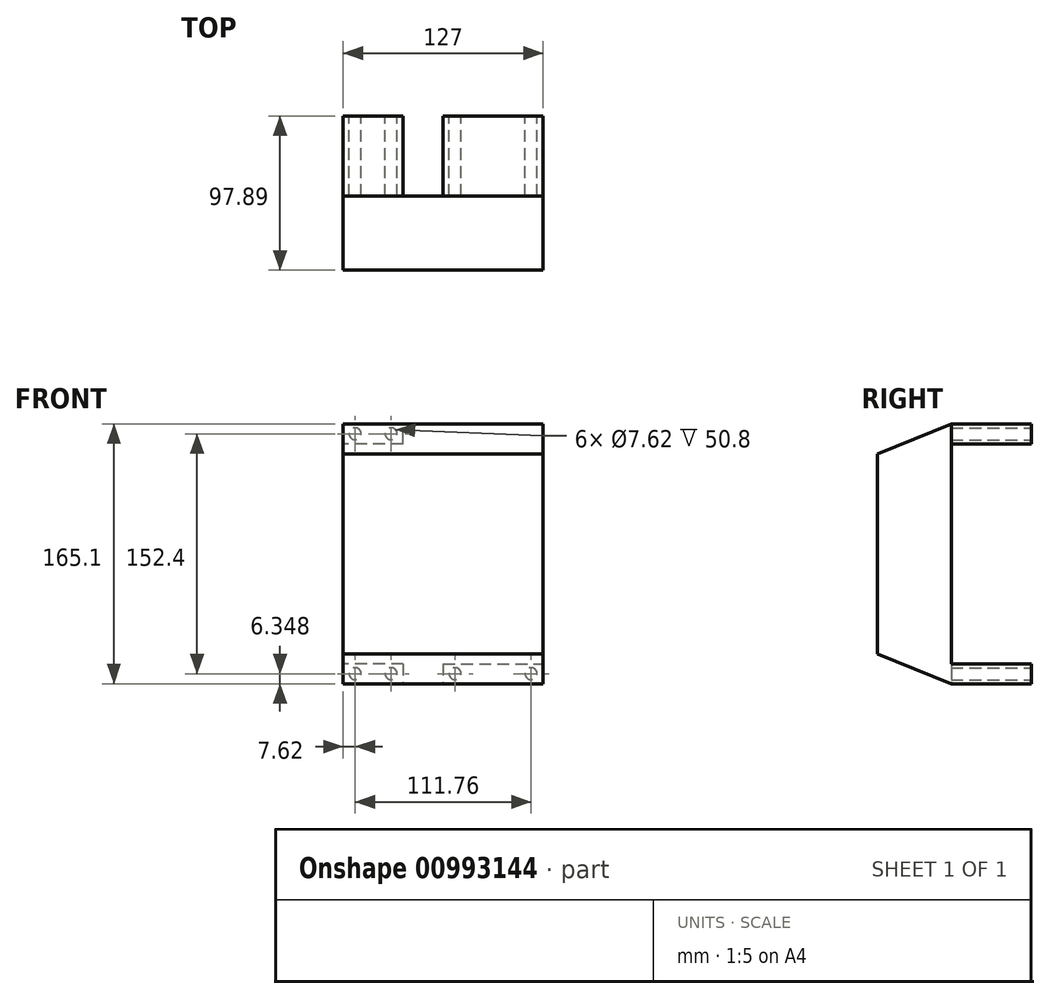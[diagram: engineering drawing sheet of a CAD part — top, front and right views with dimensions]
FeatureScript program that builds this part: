
annotation { "Feature Type Name" : "Feature", "Feature Type Description" : "" }
export const myFeature = defineFeature(function(context is Context, id is Id, definition is map)
    precondition{}
    {
        {
            var Q0;
            Q0=qCreatedBy(makeId("Right.planeOp"),FACE);
            var sketch = newSketch(context, id + "F0", { "sketchPlane" : qUnion([Q0])});
            skLineSegment(sketch, "E0", {"start": v(37.9, 107.88) * mm, "end": v(37.9, -57.22) * mm});
            skLineSegment(sketch, "E1", {"start": v(37.9, 107.88) * mm, "end": v(-9.2, 88.83) * mm});
            skLineSegment(sketch, "E2", {"start": v(-9.2, 88.83) * mm, "end": v(-9.2, -38.17) * mm});
            skLineSegment(sketch, "E3", {"start": v(-9.2, -38.17) * mm, "end": v(37.9, -57.22) * mm});
            skLineSegment(sketch, "E4.bottom", {"start": v(37.9, -57.22) * mm, "end": v(88.7, -57.22) * mm});
            skLineSegment(sketch, "E4.top", {"start": v(37.9, -44.52) * mm, "end": v(88.7, -44.52) * mm});
            skLineSegment(sketch, "E4.left", {"start": v(37.9, -57.22) * mm, "end": v(37.9, -44.52) * mm});
            skLineSegment(sketch, "E4.right", {"start": v(88.7, -57.22) * mm, "end": v(88.7, -44.52) * mm});
            skSolve(sketch);
        }
        {
            var Q0;
            Q0=makeQuery(id+"F0.imprint","IMPRINT",FACE,{"disambiguationData":[TD([[makeQuery(id+"F0.imprint","IMPRINT",EDGE,{"derivedFrom":sQuery(id+"F0.wireOp",EDGE,"E0")}),-1.0]])]});
            extrude(context, id + "F1", {"entities" : qUnion([Q0]), "depth" : 127 * mm, "offsetDistance" : 25.4 * mm});
        }
        {
            var Q0;
            Q0=makeQuery(id+"F0.imprint","IMPRINT",FACE,{"disambiguationData":[TD([[makeQuery(id+"F0.imprint","IMPRINT",EDGE,{"derivedFrom":sQuery(id+"F0.wireOp",EDGE,"E4.bottom")}),1.0]])]});
            extrude(context, id + "F2", {"entities" : qUnion([Q0]), "operationType" : NewBodyOperationType.ADD, "depth" : 38.1 * mm, "offsetDistance" : 25.4 * mm});
        }
        {
            var Q0;
            Q0=makeQuery(id+"F1.opExtrude","SWEPT_FACE",FACE,{"disambiguationData":[OSD([sQuery(id+"F0.wireOp",EDGE,"E0"),sQuery(id+"F0.wireOp",EDGE,"E4.left")])]});
            var sketch = newSketch(context, id + "F3", { "sketchPlane" : qUnion([Q0])});
            skLineSegment(sketch, "E5.bottom", {"start": v(-63.5, -44.52) * mm, "end": v(-127, -44.52) * mm});
            skLineSegment(sketch, "E5.top", {"start": v(-63.5, -57.22) * mm, "end": v(-127, -57.22) * mm});
            skLineSegment(sketch, "E5.left", {"start": v(-63.5, -44.52) * mm, "end": v(-63.5, -57.22) * mm});
            skLineSegment(sketch, "E5.right", {"start": v(-127, -44.52) * mm, "end": v(-127, -57.22) * mm});
            skLineSegment(sketch, "E6.bottom", {"start": v(-38.1, 95.18) * mm, "end": v(0, 95.18) * mm});
            skLineSegment(sketch, "E6.top", {"start": v(-38.1, 107.88) * mm, "end": v(0, 107.88) * mm});
            skLineSegment(sketch, "E6.left", {"start": v(-38.1, 95.18) * mm, "end": v(-38.1, 107.88) * mm});
            skLineSegment(sketch, "E6.right", {"start": v(0, 95.18) * mm, "end": v(0, 107.88) * mm});
            skSolve(sketch);
        }
        {
            var Q0;
            Q0=makeQuery(id+"F3.imprint","IMPRINT",FACE,{"disambiguationData":[TD([[makeQuery(id+"F3.imprint","IMPRINT",EDGE,{"derivedFrom":sQuery(id+"F3.wireOp",EDGE,"E5.bottom")}),1.0]])]});
            var Q1;
            Q1=makeQuery(id+"F3.imprint","IMPRINT",FACE,{"disambiguationData":[TD([[makeQuery(id+"F3.imprint","IMPRINT",EDGE,{"derivedFrom":sQuery(id+"F3.wireOp",EDGE,"tAGeQwlt-6s59-XwvX-LVoE-sqzA5QCWcFZO.bottom")}),-1.0]])]});
            var Q2;
            Q2=makeQuery(id+"F3.imprint","IMPRINT",FACE,{"disambiguationData":[TD([[makeQuery(id+"F3.imprint","IMPRINT",EDGE,{"derivedFrom":sQuery(id+"F3.wireOp",EDGE,"E6.bottom")}),1.0]])]});
            extrude(context, id + "F4", {"entities" : qUnion([Q0, Q1, Q2]), "operationType" : NewBodyOperationType.ADD, "depth" : 50.8 * mm, "offsetDistance" : 25.4 * mm});
        }
        {
            var Q0;
            Q0=makeQuery(id+"F4.opExtrude","CAP_FACE",FACE,{"disambiguationData":[OSD([sQuery(id+"F3.wireOp",EDGE,"E6.bottom"),sQuery(id+"F3.wireOp",EDGE,"E6.top"),sQuery(id+"F3.wireOp",EDGE,"E6.left"),sQuery(id+"F3.wireOp",EDGE,"E6.right")])],"isStart":false});
            var sketch = newSketch(context, id + "F5", { "sketchPlane" : qUnion([Q0])});
            skCircle(sketch, "E7", {"center": v(-30.48, 101.53) * mm, "radius": 3.81 * mm});
            skPoint(sketch, "E7.centerSnap0", {"position": v(-38.1, 101.53) * mm});
            skCircle(sketch, "E8", {"center": v(-7.62, 101.53) * mm, "radius": 3.81 * mm});
            skSolve(sketch);
        }
        {
            var Q0;
            Q0=makeQuery(id+"F5.imprint","IMPRINT",FACE,{"disambiguationData":[TD([[makeQuery(id+"F5.imprint","IMPRINT",EDGE,{"derivedFrom":sQuery(id+"F5.wireOp",EDGE,"E8")}),1.0]])]});
            var Q1;
            Q1=makeQuery(id+"F5.imprint","IMPRINT",FACE,{"disambiguationData":[TD([[makeQuery(id+"F5.imprint","IMPRINT",EDGE,{"derivedFrom":sQuery(id+"F5.wireOp",EDGE,"E7")}),1.0]])]});
            extrude(context, id + "F6", {"entities" : qUnion([Q0, Q1]), "operationType" : NewBodyOperationType.REMOVE, "oppositeDirection" : true, "depth" : 50.8 * mm, "offsetDistance" : 25.4 * mm});
        }
        {
            var Q0;
            Q0=makeQuery(id+"F2.opExtrude","SWEPT_FACE",FACE,{"disambiguationData":[OSD([sQuery(id+"F0.wireOp",EDGE,"E4.right")])]});
            var sketch = newSketch(context, id + "F7", { "sketchPlane" : qUnion([Q0])});
            skCircle(sketch, "E9", {"center": v(-30.48, -50.87) * mm, "radius": 3.81 * mm});
            skPoint(sketch, "E9.centerSnap0", {"position": v(-38.1, -50.87) * mm});
            skCircle(sketch, "E10", {"center": v(-7.62, -50.87) * mm, "radius": 3.81 * mm});
            skSolve(sketch);
        }
        {
            var Q0;
            Q0=makeQuery(id+"F7.imprint","IMPRINT",FACE,{"disambiguationData":[TD([[makeQuery(id+"F7.imprint","IMPRINT",EDGE,{"derivedFrom":sQuery(id+"F7.wireOp",EDGE,"E9")}),1.0]])]});
            var Q1;
            Q1=makeQuery(id+"F7.imprint","IMPRINT",FACE,{"disambiguationData":[TD([[makeQuery(id+"F7.imprint","IMPRINT",EDGE,{"derivedFrom":sQuery(id+"F7.wireOp",EDGE,"E10")}),1.0]])]});
            extrude(context, id + "F8", {"entities" : qUnion([Q0, Q1]), "operationType" : NewBodyOperationType.REMOVE, "oppositeDirection" : true, "depth" : 50.8 * mm, "offsetDistance" : 25.4 * mm});
        }
        {
            var Q0;
            Q0=makeQuery(id+"F4.opExtrude","CAP_FACE",FACE,{"disambiguationData":[OSD([sQuery(id+"F3.wireOp",EDGE,"E5.bottom"),sQuery(id+"F3.wireOp",EDGE,"E5.top"),sQuery(id+"F3.wireOp",EDGE,"E5.left"),sQuery(id+"F3.wireOp",EDGE,"E5.right")])],"isStart":false});
            var sketch = newSketch(context, id + "F9", { "sketchPlane" : qUnion([Q0])});
            skCircle(sketch, "E11", {"center": v(-71.12, -50.87) * mm, "radius": 3.81 * mm});
            skPoint(sketch, "E11.centerSnap0", {"position": v(-63.5, -50.87) * mm});
            skCircle(sketch, "E12", {"center": v(-119.38, -50.87) * mm, "radius": 3.81 * mm});
            skPoint(sketch, "E12.centerSnap0", {"position": v(-127, -50.87) * mm});
            skSolve(sketch);
        }
        {
            var Q0;
            Q0=makeQuery(id+"F9.imprint","IMPRINT",FACE,{"disambiguationData":[TD([[makeQuery(id+"F9.imprint","IMPRINT",EDGE,{"derivedFrom":sQuery(id+"F9.wireOp",EDGE,"E11")}),1.0]])]});
            var Q1;
            Q1=makeQuery(id+"F9.imprint","IMPRINT",FACE,{"disambiguationData":[TD([[makeQuery(id+"F9.imprint","IMPRINT",EDGE,{"derivedFrom":sQuery(id+"F9.wireOp",EDGE,"E12")}),1.0]])]});
            extrude(context, id + "F10", {"entities" : qUnion([Q0, Q1]), "operationType" : NewBodyOperationType.REMOVE, "oppositeDirection" : true, "depth" : 50.8 * mm, "offsetDistance" : 25.4 * mm});
        }
    });
